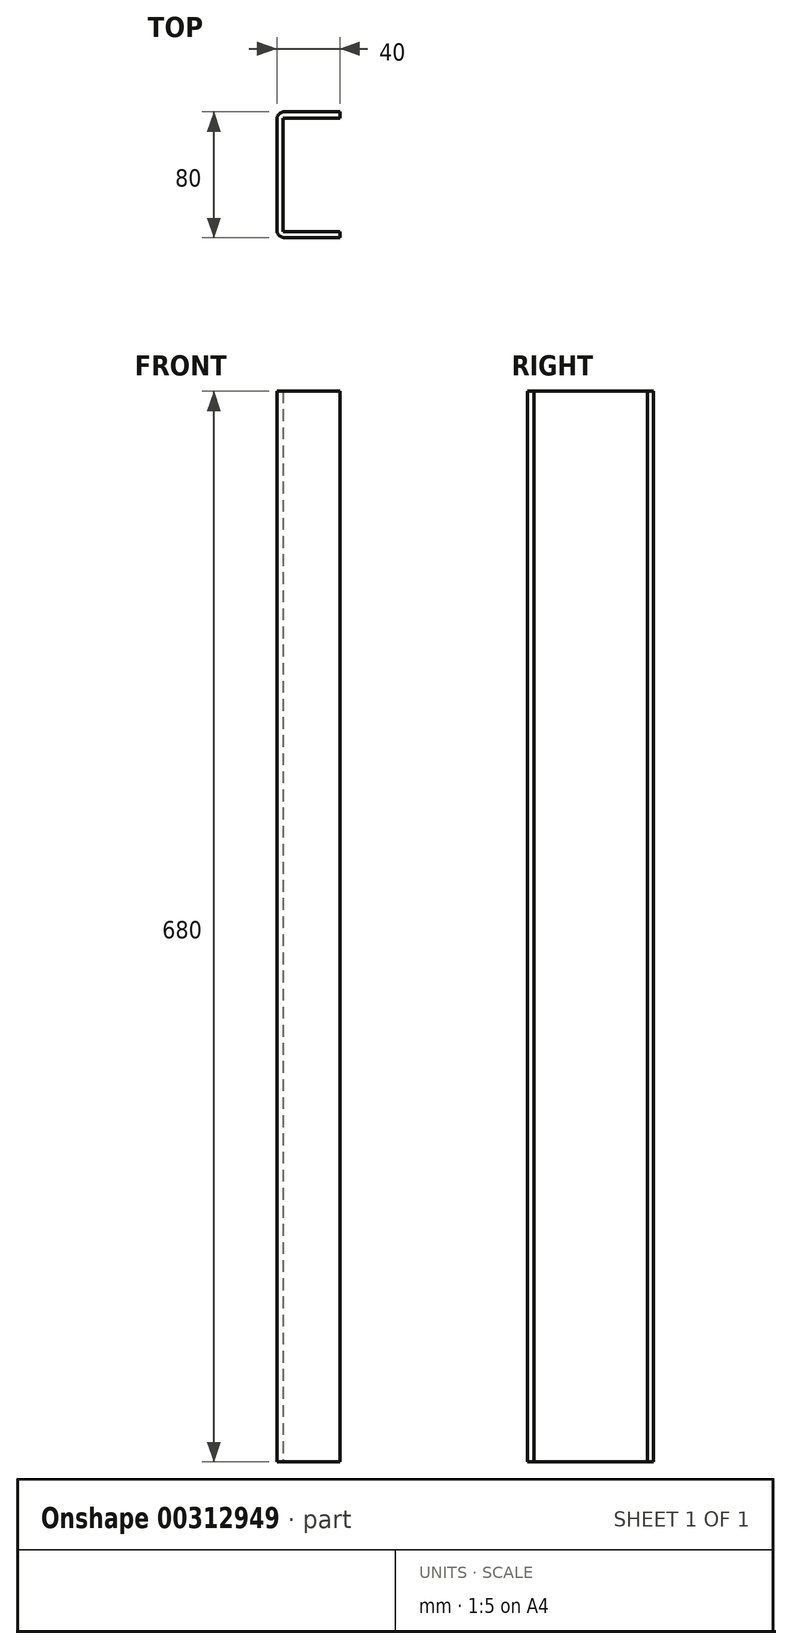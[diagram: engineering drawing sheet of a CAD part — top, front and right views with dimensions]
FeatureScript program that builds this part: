
annotation { "Feature Type Name" : "Feature", "Feature Type Description" : "" }
export const myFeature = defineFeature(function(context is Context, id is Id, definition is map)
    precondition{}
    {
        {
            var Q0;
            Q0=qCreatedBy(makeId("Top.planeOp"),FACE);
            var sketch = newSketch(context, id + "F0", { "sketchPlane" : qUnion([Q0])});
            skLineSegment(sketch, "E0.bottom", {"start": v(20, 40) * mm, "end": v(-20, 40) * mm});
            skLineSegment(sketch, "E0.top", {"start": v(20, -40) * mm, "end": v(-20, -40) * mm});
            skLineSegment(sketch, "E0.left", {"start": v(20, 40) * mm, "end": v(20, 36) * mm});
            skLineSegment(sketch, "E0.right", {"start": v(-20, 40) * mm, "end": v(-20, -40) * mm});
            skPoint(sketch, "E0.middle", {"position": v(0, 0) * mm});
            skLineSegment(sketch, "E1", {"start": v(20, -36) * mm, "end": v(-16, -36) * mm});
            skLineSegment(sketch, "E2", {"start": v(-16, -36) * mm, "end": v(-16, 36) * mm});
            skLineSegment(sketch, "E3", {"start": v(-16, 36) * mm, "end": v(20, 36) * mm});
            skLineSegment(sketch, "E4.trimOffspring", {"start": v(20, -36) * mm, "end": v(20, -40) * mm});
            skSolve(sketch);
        }
        {
            var Q0;
            Q0=qSketchRegion(id+"F0",true);
            extrude(context, id + "F1", {"entities" : qUnion([Q0]), "depth" : 680 * mm});
        }
        {
            var Q0;
            Q0=makeQuery(id+"F1.opExtrude","SWEPT_EDGE",EDGE,{"disambiguationData":[OSD([sQuery(id+"F0.wireOp",EDGE,"E0.bottom"),sQuery(id+"F0.wireOp",EDGE,"E0.right")])]});
            var Q1;
            Q1=makeQuery(id+"F1.opExtrude","SWEPT_EDGE",EDGE,{"disambiguationData":[OSD([sQuery(id+"F0.wireOp",EDGE,"E0.top"),sQuery(id+"F0.wireOp",EDGE,"E0.right")])]});
            fillet(context, id + "F2", {"entities" : qUnion([Q0, Q1]), "radius" : 5 * mm, "tangentPropagation" : true, "allowEdgeOverflow" : false});
        }
    });
